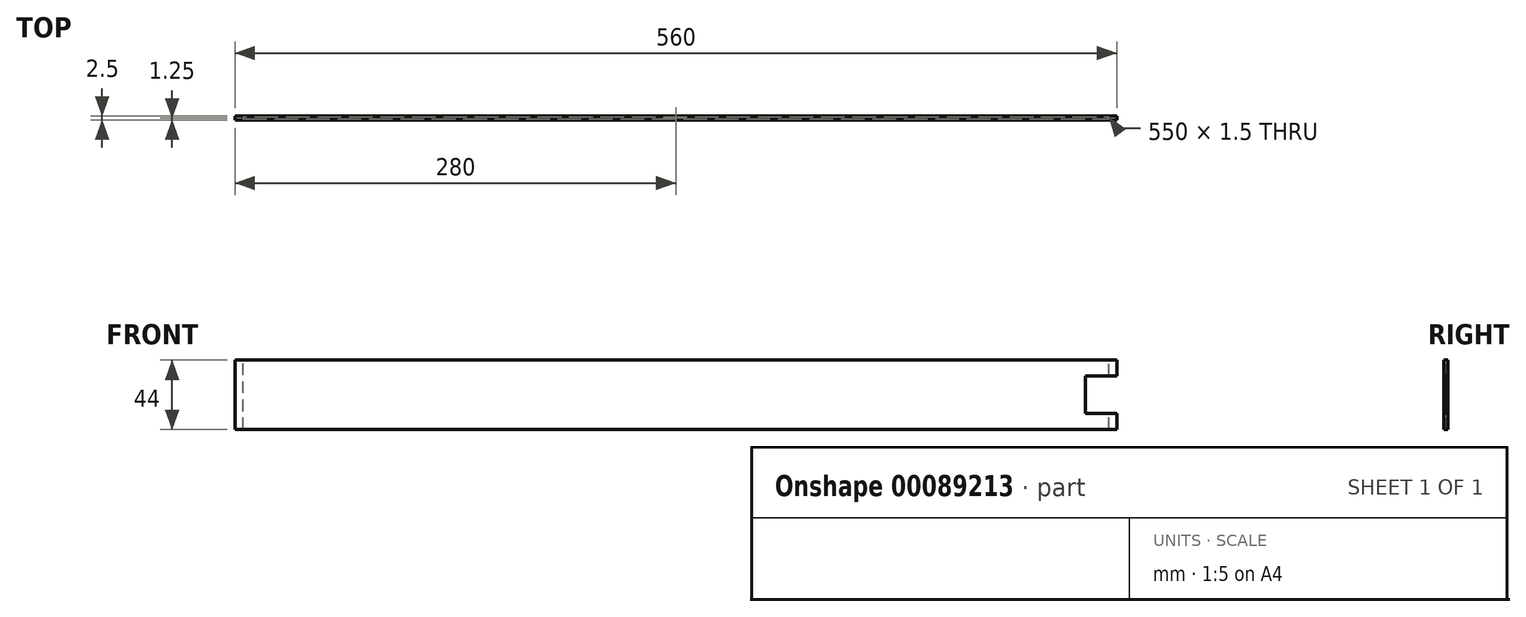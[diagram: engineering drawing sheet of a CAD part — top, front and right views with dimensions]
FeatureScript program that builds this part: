
annotation { "Feature Type Name" : "Feature", "Feature Type Description" : "" }
export const myFeature = defineFeature(function(context is Context, id is Id, definition is map)
    precondition{}
    {
        {
            var Q0;
            Q0=qCreatedBy(makeId("Front.planeOp"),FACE);
            var sketch = newSketch(context, id + "F0", { "sketchPlane" : qUnion([Q0])});
            skLineSegment(sketch, "E0.bottom", {"start": v(0, 0) * mm, "end": v(560, 0) * mm});
            skLineSegment(sketch, "E0.top", {"start": v(0, 44) * mm, "end": v(560, 44) * mm});
            skLineSegment(sketch, "E0.left", {"start": v(0, 0) * mm, "end": v(0, 44) * mm});
            skLineSegment(sketch, "E0.right", {"start": v(560, 0) * mm, "end": v(560, 44) * mm});
            skSolve(sketch);
        }
        {
            var Q0;
            Q0=makeQuery(id+"F0.imprint","IMPRINT",FACE,{"disambiguationData":[TD([[makeQuery(id+"F0.imprint","IMPRINT",EDGE,{"derivedFrom":sQuery(id+"F0.wireOp",EDGE,"E0.bottom")}),1.0]])]});
            extrude(context, id + "F1", {"entities" : qUnion([Q0]), "depth" : 0.5 * mm});
        }
        {
            var Q0;
            Q0=makeQuery(id+"F1.opExtrude","CAP_FACE",FACE,{"disambiguationData":[OSD([sQuery(id+"F0.wireOp",EDGE,"E0.bottom"),sQuery(id+"F0.wireOp",EDGE,"E0.top"),sQuery(id+"F0.wireOp",EDGE,"E0.left"),sQuery(id+"F0.wireOp",EDGE,"E0.right")])],"isStart":true});
            var sketch = newSketch(context, id + "F2", { "sketchPlane" : qUnion([Q0])});
            skLineSegment(sketch, "E1.bottom", {"start": v(-560, 0) * mm, "end": v(-555, 0) * mm});
            skLineSegment(sketch, "E1.top", {"start": v(-560, 44) * mm, "end": v(-555, 44) * mm});
            skLineSegment(sketch, "E1.left", {"start": v(-560, 0) * mm, "end": v(-560, 44) * mm});
            skLineSegment(sketch, "E1.right", {"start": v(-555, 0) * mm, "end": v(-555, 44) * mm});
            skLineSegment(sketch, "E2.bottom", {"start": v(0, 0) * mm, "end": v(-5, 0) * mm});
            skLineSegment(sketch, "E2.top", {"start": v(0, 44) * mm, "end": v(-5, 44) * mm});
            skLineSegment(sketch, "E2.left", {"start": v(0, 0) * mm, "end": v(0, 44) * mm});
            skLineSegment(sketch, "E2.right", {"start": v(-5, 0) * mm, "end": v(-5, 44) * mm});
            skSolve(sketch);
        }
        {
            var Q0;
            Q0 = qSketchRegion(id + "F2", true);
            extrude(context, id + "F3", {"entities" : qUnion([Q0]), "operationType" : NewBodyOperationType.ADD, "depth" : 1.5 * mm});
        }
        {
            var Q0;
            Q0=makeQuery(id+"F3.opExtrude","CAP_FACE",FACE,{"disambiguationData":[OSD([sQuery(id+"F2.wireOp",EDGE,"E1.bottom"),sQuery(id+"F2.wireOp",EDGE,"E1.top"),sQuery(id+"F2.wireOp",EDGE,"E1.left"),sQuery(id+"F2.wireOp",EDGE,"E1.right")])],"isStart":false});
            var sketch = newSketch(context, id + "F4", { "sketchPlane" : qUnion([Q0])});
            skLineSegment(sketch, "E3.bottom", {"start": v(-560, 0) * mm, "end": v(0, 0) * mm});
            skLineSegment(sketch, "E3.top", {"start": v(-560, 44) * mm, "end": v(0, 44) * mm});
            skLineSegment(sketch, "E3.left", {"start": v(-560, 0) * mm, "end": v(-560, 44) * mm});
            skLineSegment(sketch, "E3.right", {"start": v(0, 0) * mm, "end": v(0, 44) * mm});
            skSolve(sketch);
        }
        {
            var Q0;
            Q0 = qSketchRegion(id + "F4", true);
            extrude(context, id + "F5", {"entities" : qUnion([Q0]), "operationType" : NewBodyOperationType.ADD, "depth" : 0.5 * mm});
        }
        {
            var Q0;
            Q0=makeQuery(id+"F5.opExtrude","CAP_FACE",FACE,{"disambiguationData":[OSD([sQuery(id+"F4.wireOp",EDGE,"E3.bottom"),sQuery(id+"F4.wireOp",EDGE,"E3.top"),sQuery(id+"F4.wireOp",EDGE,"E3.left"),sQuery(id+"F4.wireOp",EDGE,"E3.right")])],"isStart":false});
            var sketch = newSketch(context, id + "F6", { "sketchPlane" : qUnion([Q0])});
            skLineSegment(sketch, "E4.bottom", {"start": v(-560, 34) * mm, "end": v(-540, 34) * mm});
            skLineSegment(sketch, "E4.top", {"start": v(-560, 10) * mm, "end": v(-540, 10) * mm});
            skLineSegment(sketch, "E4.left", {"start": v(-560, 34) * mm, "end": v(-560, 10) * mm});
            skLineSegment(sketch, "E4.right", {"start": v(-540, 34) * mm, "end": v(-540, 10) * mm});
            skSolve(sketch);
        }
        {
            var Q0;
            Q0=makeQuery(id+"F6.imprint","IMPRINT",FACE,{"disambiguationData":[TD([[makeQuery(id+"F6.imprint","IMPRINT",EDGE,{"derivedFrom":sQuery(id+"F6.wireOp",EDGE,"E4.bottom")}),-1.0]])]});
            extrude(context, id + "F7", {"entities" : qUnion([Q0]), "operationType" : NewBodyOperationType.REMOVE, "endBound" : BoundingType.THROUGH_ALL, "oppositeDirection" : true, "depth" : 2 * mm});
        }
    });
